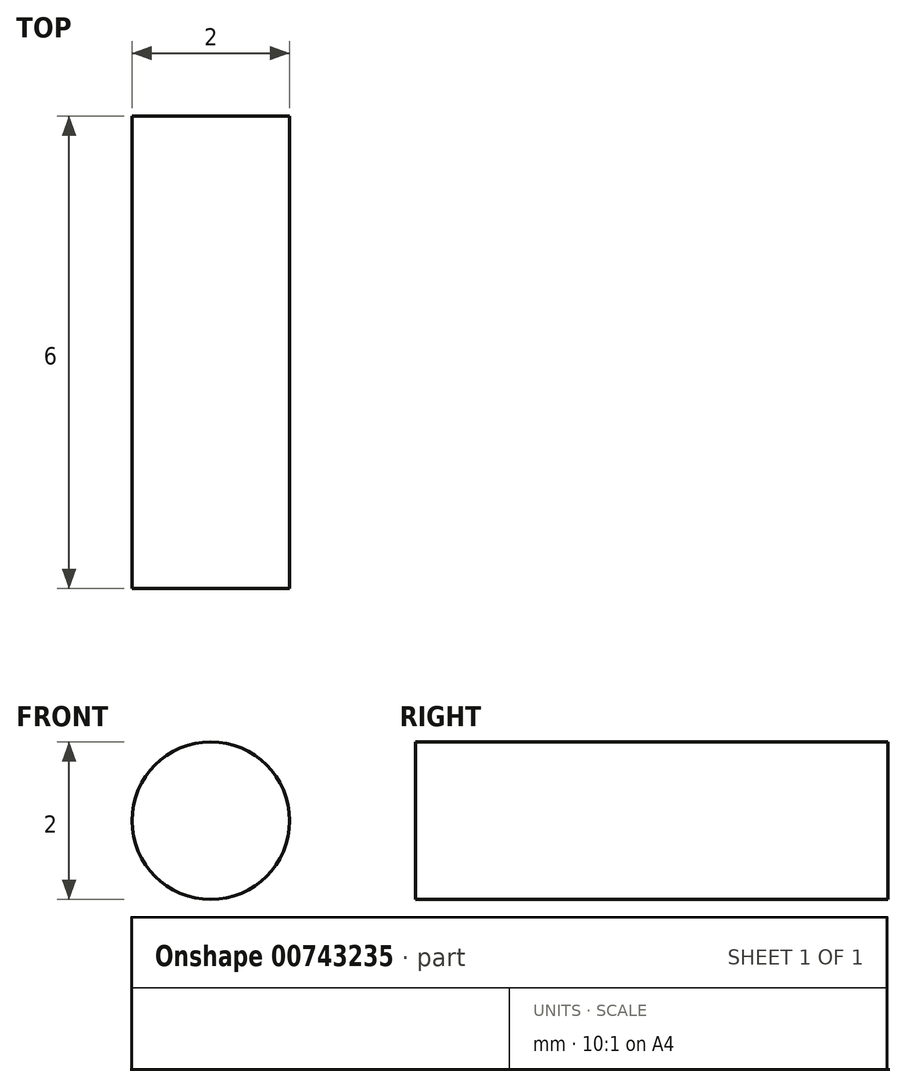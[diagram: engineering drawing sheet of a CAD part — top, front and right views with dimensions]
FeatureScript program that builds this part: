
annotation { "Feature Type Name" : "Feature", "Feature Type Description" : "" }
export const myFeature = defineFeature(function(context is Context, id is Id, definition is map)
    precondition{}
    {
        {
            var Q0;
            Q0=qCreatedBy(makeId("Front.planeOp"),FACE);
            var sketch = newSketch(context, id + "F0", { "sketchPlane" : qUnion([Q0])});
            skCircle(sketch, "E0", {"center": v(0, 0) * mm, "radius": 1 * mm});
            skSolve(sketch);
        }
        {
            var Q0;
            Q0=qSketchRegion(id+"F0",true);
            extrude(context, id + "F1", {"entities" : qUnion([Q0]), "depth" : 6 * mm, "offsetDistance" : 25 * mm});
        }
    });
